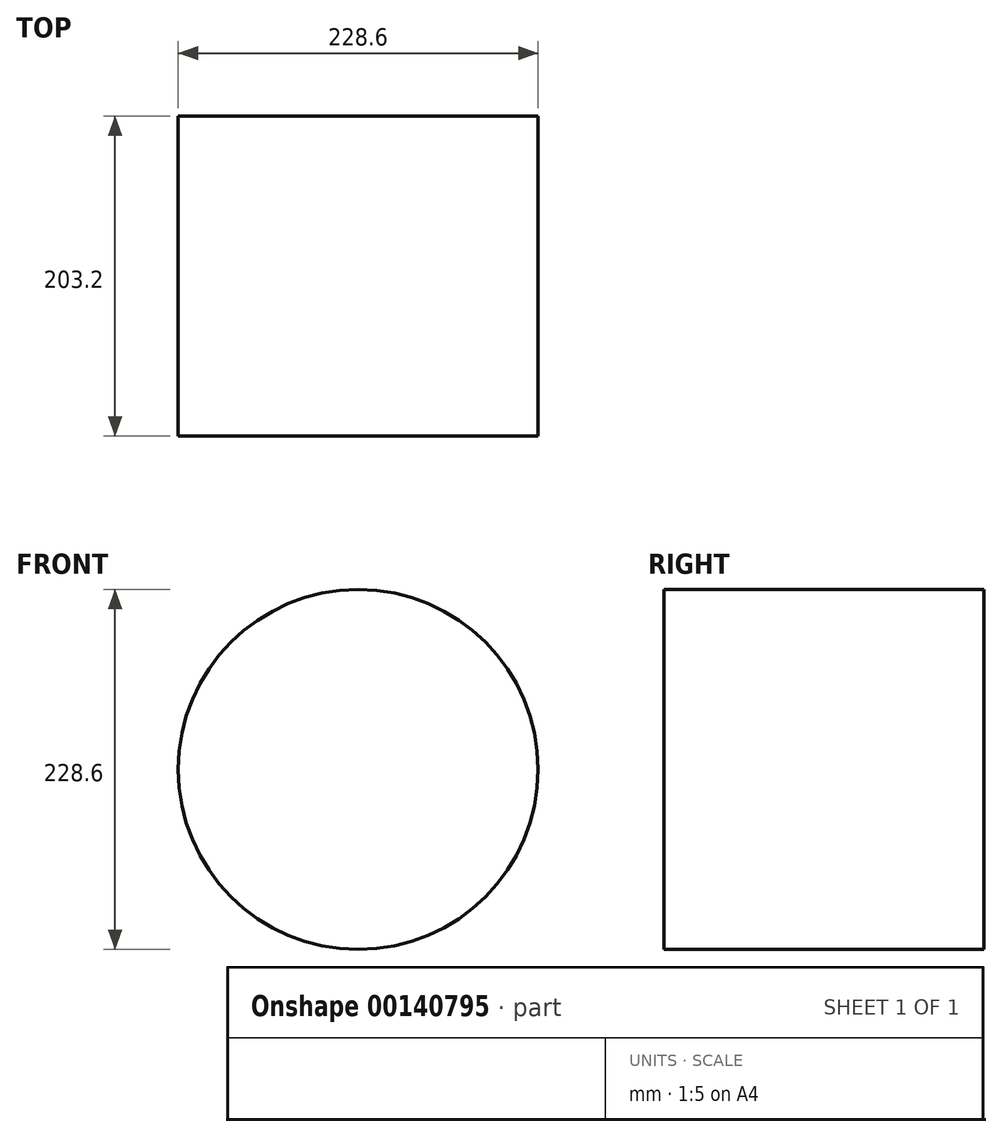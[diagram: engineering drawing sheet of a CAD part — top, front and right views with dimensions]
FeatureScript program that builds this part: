
annotation { "Feature Type Name" : "Feature", "Feature Type Description" : "" }
export const myFeature = defineFeature(function(context is Context, id is Id, definition is map)
    precondition{}
    {
        {
            var Q0;
            Q0=qCreatedBy(makeId("Front.planeOp"),FACE);
            var sketch = newSketch(context, id + "F0", { "sketchPlane" : qUnion([Q0])});
            skCircle(sketch, "E0", {"center": v(0, 0) * mm, "radius": 114.3 * mm});
            skSolve(sketch);
        }
        {
            var Q0;
            Q0=makeQuery(id+"F0.imprint","IMPRINT",FACE,{"disambiguationData":[TD([[makeQuery(id+"F0.imprint","IMPRINT",EDGE,{"derivedFrom":sQuery(id+"F0.wireOp",EDGE,"E0")}),1.0]])]});
            extrude(context, id + "F1", {"entities" : qUnion([Q0]), "depth" : 203.2 * mm});
        }
    });
